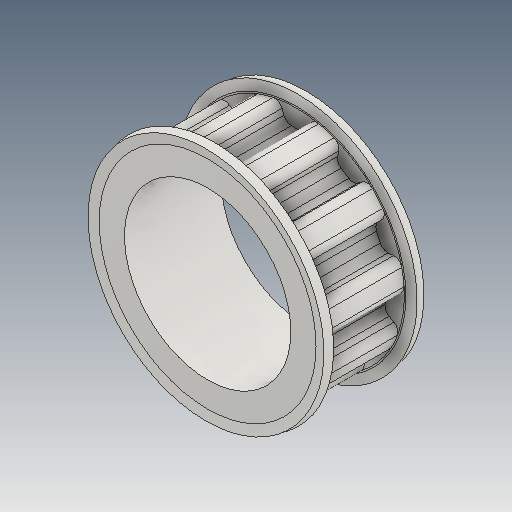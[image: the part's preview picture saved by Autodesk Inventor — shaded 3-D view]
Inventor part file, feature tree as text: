
AUTODESK INVENTOR PART (.ipt)
format: ipt  version: 2020.3 (Build 243373010, 373A)  size: 345,088 bytes
history: native  units: mm (DEFAULTED — no unit token found)
features: other x3, extrude x3, fillet x1, pattern_circular x1, sketch x1
ambient origin geometry x8: Origin, YZ Plane, XZ Plane, XY Plane, X Axis, Y Axis, Z Axis, Center Point
bodies: Solid1 (feature_tree)
feature tree (9):
  other  "Pulley Sketch"
  extrude  "Base Body"  Depth=1.1684mm
  extrude  "Tooth"  Depth=1.1684mm
  fillet  "Tooth Fillet"  Radius=6.981317mm
  pattern_circular  "Teeth"  [2 undecoded]
  other  "Left flange"
  other  "Right flange"
  extrude  "Extrusion3"  Depth=12.0mm
  sketch  "Sketch2"  dims[d0=33.350918mm d1=0.381mm d2=2.667mm d3=6.981317mm d4=3.048mm d5=12.0mm d6=0.0mm d7=12.0mm d8=0.0mm d9=1.1938mm d10=1.1684mm d11=110.0mm d12=360.0deg d15=0.0mm d16=0.0mm d17=25.0mm d18=0.252mm d19=0.0mm]
note: 2 required parameter values undecoded (feature->parameter linkage not recoverable at this tier; creation-order binding heuristic only, values carry confidence <= 0.55)
